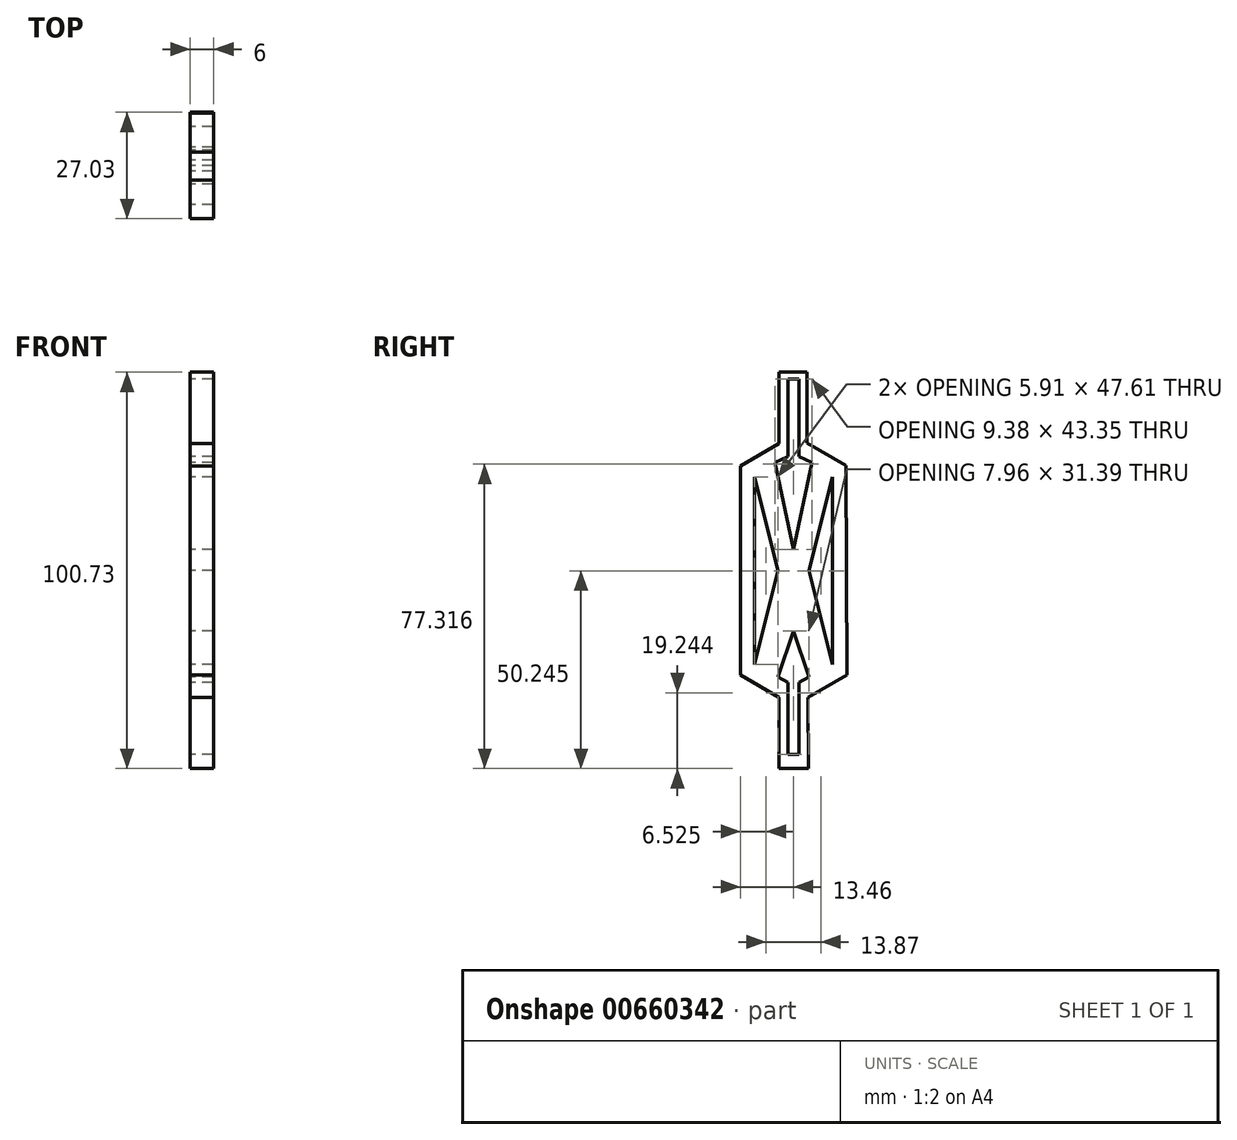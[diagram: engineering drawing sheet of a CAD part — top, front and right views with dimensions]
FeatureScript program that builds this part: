
annotation { "Feature Type Name" : "Feature", "Feature Type Description" : "" }
export const myFeature = defineFeature(function(context is Context, id is Id, definition is map)
    precondition{}
    {
        {
            var Q0;
            Q0=qCreatedBy(makeId("Right.planeOp"),FACE);
            var sketch = newSketch(context, id + "F0", { "sketchPlane" : qUnion([Q0])});
            skLineSegment(sketch, "E0", {"start": v(-3.61, 50.35) * mm, "end": v(-3.61, 32.27) * mm});
            skLineSegment(sketch, "E1", {"start": v(-3.61, 32.27) * mm, "end": v(-13.46, 26.55) * mm});
            skLineSegment(sketch, "E2", {"start": v(-3.61, -50.37) * mm, "end": v(-3.61, -32.3) * mm});
            skLineSegment(sketch, "E3", {"start": v(-13.46, -26.59) * mm, "end": v(-3.61, -32.3) * mm});
            skLineSegment(sketch, "E4", {"start": v(-13.46, 26.55) * mm, "end": v(-13.46, -26.59) * mm});
            skLineSegment(sketch, "E5.MirrorCS", {"start": v(13.36, 26.6) * mm, "end": v(13.57, -26.54) * mm});
            skLineSegment(sketch, "E6.MirrorCS", {"start": v(13.57, -26.54) * mm, "end": v(3.74, -32.28) * mm});
            skLineSegment(sketch, "E7.MirrorCS", {"start": v(3.8, -50.35) * mm, "end": v(3.74, -32.28) * mm});
            skLineSegment(sketch, "E8.MirrorCS", {"start": v(3.42, 50.36) * mm, "end": v(3.49, 32.29) * mm});
            skLineSegment(sketch, "E9.MirrorCS", {"start": v(3.49, 32.29) * mm, "end": v(13.36, 26.6) * mm});
            skLineSegment(sketch, "E10", {"start": v(-3.61, 50.35) * mm, "end": v(3.42, 50.36) * mm});
            skLineSegment(sketch, "E11", {"start": v(-3.61, -50.37) * mm, "end": v(3.8, -50.35) * mm});
            skLineSegment(sketch, "E12", {"start": v(0, 57.48) * mm, "end": v(0, -60.3) * mm, "construction": true});
            skLineSegment(sketch, "E13", {"start": v(-1.45, 48.62) * mm, "end": v(-1.45, 28.9) * mm});
            skLineSegment(sketch, "E14", {"start": v(-9.89, 23.68) * mm, "end": v(-9.89, -23.93) * mm});
            skLineSegment(sketch, "E15", {"start": v(-1.45, -28.48) * mm, "end": v(-1.45, -46.82) * mm});
            skLineSegment(sketch, "E16.MirrorCS", {"start": v(9.89, 23.68) * mm, "end": v(9.89, -23.93) * mm});
            skLineSegment(sketch, "E17.MirrorCS", {"start": v(1.45, -28.48) * mm, "end": v(1.45, -46.82) * mm});
            skLineSegment(sketch, "E18.MirrorCS", {"start": v(1.45, 48.62) * mm, "end": v(1.45, 28.9) * mm});
            skLineSegment(sketch, "E19", {"start": v(-1.45, 48.62) * mm, "end": v(1.45, 48.62) * mm});
            skLineSegment(sketch, "E20", {"start": v(-1.45, -46.82) * mm, "end": v(1.45, -46.82) * mm});
            skLineSegment(sketch, "E21", {"start": v(-1.45, 28.9) * mm, "end": v(-4.69, 27.38) * mm});
            skLineSegment(sketch, "E22", {"start": v(-4.69, 27.38) * mm, "end": v(0, 5.27) * mm});
            skLineSegment(sketch, "E23", {"start": v(-9.89, 23.68) * mm, "end": v(-3.98, 0) * mm});
            skLineSegment(sketch, "E24", {"start": v(-3.98, 0) * mm, "end": v(-9.89, -23.93) * mm});
            skLineSegment(sketch, "E25", {"start": v(-3.98, -27.12) * mm, "end": v(0, -15.43) * mm});
            skLineSegment(sketch, "E26.MirrorCS", {"start": v(3.98, -27.12) * mm, "end": v(0, -15.43) * mm});
            skLineSegment(sketch, "E27.MirrorCS", {"start": v(3.98, 0) * mm, "end": v(9.89, -23.93) * mm});
            skLineSegment(sketch, "E28.MirrorCS", {"start": v(9.89, 23.68) * mm, "end": v(3.98, 0) * mm});
            skLineSegment(sketch, "E29.MirrorCS", {"start": v(4.69, 27.38) * mm, "end": v(0, 5.27) * mm});
            skLineSegment(sketch, "E30", {"start": v(-3.98, -27.12) * mm, "end": v(-1.45, -28.48) * mm});
            skLineSegment(sketch, "E31.MirrorCS", {"start": v(3.98, -27.12) * mm, "end": v(1.45, -28.48) * mm});
            skLineSegment(sketch, "E32.MirrorCS", {"start": v(1.45, 28.9) * mm, "end": v(4.69, 27.38) * mm});
            skSolve(sketch);
        }
        {
            var Q0;
            Q0 = qSketchRegion(id + "F0", true);
            extrude(context, id + "F1", {"entities" : qUnion([Q0]), "depth" : 4 * mm, "offsetDistance" : 25 * mm});
        }
        {
            var Q0;
            Q0 = qSketchRegion(id + "F0", true);
            extrude(context, id + "F2", {"entities" : qUnion([Q0]), "operationType" : NewBodyOperationType.ADD, "depth" : 6 * mm, "offsetDistance" : 25 * mm});
        }
    });
